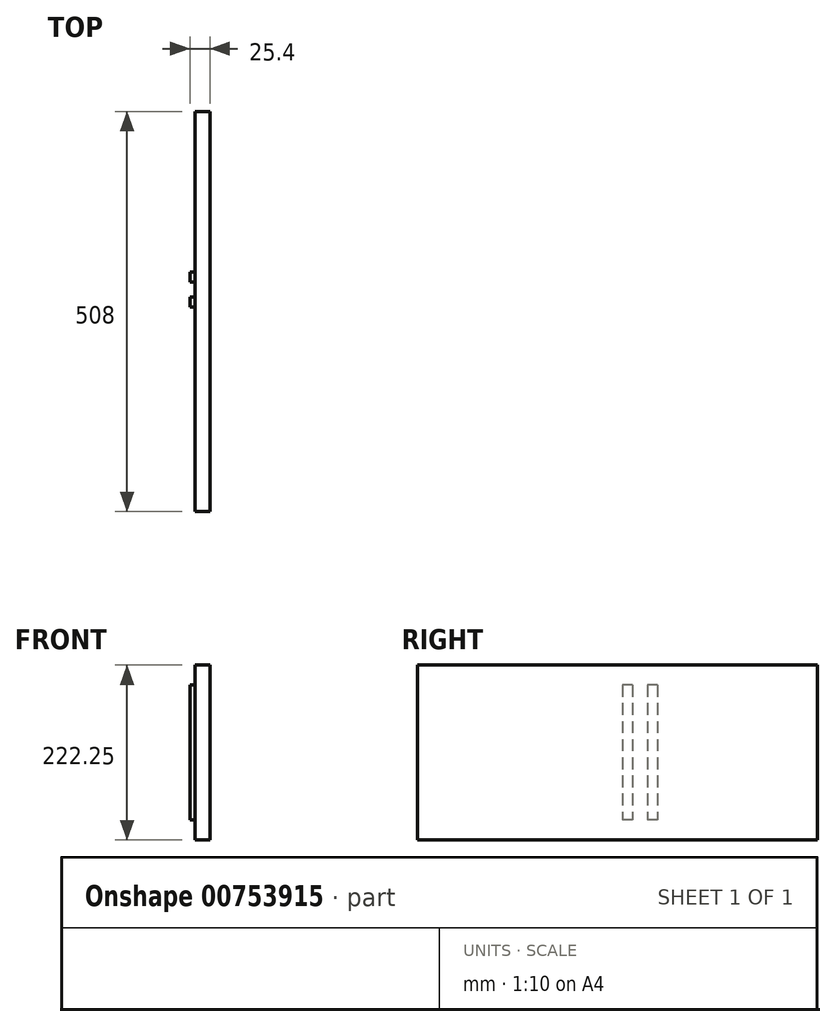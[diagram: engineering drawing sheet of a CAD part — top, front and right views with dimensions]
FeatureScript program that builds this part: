
annotation { "Feature Type Name" : "Feature", "Feature Type Description" : "" }
export const myFeature = defineFeature(function(context is Context, id is Id, definition is map)
    precondition{}
    {
        {
            var Q0;
            Q0=qCreatedBy(makeId("Right.planeOp"),FACE);
            var sketch = newSketch(context, id + "F0", { "sketchPlane" : qUnion([Q0])});
            skLineSegment(sketch, "E0.bottom", {"start": v(254, -111.12) * mm, "end": v(-254, -111.13) * mm});
            skLineSegment(sketch, "E0.top", {"start": v(254, 111.13) * mm, "end": v(-254, 111.12) * mm});
            skLineSegment(sketch, "E0.left", {"start": v(254, -111.12) * mm, "end": v(254, 111.13) * mm});
            skLineSegment(sketch, "E0.right", {"start": v(-254, -111.13) * mm, "end": v(-254, 111.12) * mm});
            skPoint(sketch, "E0.middle", {"position": v(0, 0) * mm});
            skLineSegment(sketch, "E1.0", {"start": v(253.65, 85.73) * mm, "end": v(-254, 85.72) * mm});
            skLineSegment(sketch, "E2.0", {"start": v(254, -85.72) * mm, "end": v(-254, -85.73) * mm});
            skLineSegment(sketch, "E3", {"start": v(253.65, 85.73) * mm, "end": v(50.45, 85.73) * mm});
            skLineSegment(sketch, "E4", {"start": v(50.45, 85.73) * mm, "end": v(37.75, 85.73) * mm});
            skLineSegment(sketch, "E5", {"start": v(37.75, 85.73) * mm, "end": v(18.7, 85.73) * mm});
            skLineSegment(sketch, "E6", {"start": v(18.7, 85.73) * mm, "end": v(6, 85.73) * mm});
            skLineSegment(sketch, "E7.bottom", {"start": v(6, 85.73) * mm, "end": v(18.7, 85.73) * mm});
            skLineSegment(sketch, "E7.top", {"start": v(6, -85.73) * mm, "end": v(18.7, -85.73) * mm});
            skLineSegment(sketch, "E7.left", {"start": v(6, 85.73) * mm, "end": v(6, -85.73) * mm});
            skLineSegment(sketch, "E7.right", {"start": v(18.7, 85.73) * mm, "end": v(18.7, -85.73) * mm});
            skLineSegment(sketch, "E8.bottom", {"start": v(37.75, 85.73) * mm, "end": v(50.45, 85.73) * mm});
            skLineSegment(sketch, "E8.top", {"start": v(37.75, -85.73) * mm, "end": v(50.45, -85.73) * mm});
            skLineSegment(sketch, "E8.left", {"start": v(37.75, 85.73) * mm, "end": v(37.75, -85.73) * mm});
            skLineSegment(sketch, "E8.right", {"start": v(50.45, 85.73) * mm, "end": v(50.45, -85.73) * mm});
            skSolve(sketch);
        }
        {
            var Q0;
            {var subQ0=sQuery(id+"F0.wireOp",EDGE,"E7.left");Q0=makeQuery(id+"F0.imprint","IMPRINT",FACE,{"disambiguationData":[TD([[makeQuery(id+"F0.imprint","IMPRINT",EDGE,{"derivedFrom":subQ0}),1.0]])]});}
            var Q1;
            {var subQ0=sQuery(id+"F0.wireOp",EDGE,"E8.left");Q1=makeQuery(id+"F0.imprint","IMPRINT",FACE,{"disambiguationData":[TD([[makeQuery(id+"F0.imprint","IMPRINT",EDGE,{"derivedFrom":subQ0}),1.0]])]});}
            extrude(context, id + "F1", {"entities" : qUnion([Q0, Q1]), "oppositeDirection" : true, "depth" : 6.35 * mm, "offsetDistance" : 25.4 * mm});
        }
        {
            var Q0;
            {var subQ5=sQuery(id+"F0.wireOp",EDGE,"E0.top");Q0=makeQuery(id+"F0.imprint","IMPRINT",FACE,{"disambiguationData":[TD([[makeQuery(id+"F0.imprint","IMPRINT",EDGE,{"derivedFrom":subQ5}),1.0]])]});}
            var Q1;
            {var subQ5=sQuery(id+"F0.wireOp",EDGE,"E7.left");Q1=makeQuery(id+"F0.imprint","IMPRINT",FACE,{"disambiguationData":[TD([[makeQuery(id+"F0.imprint","IMPRINT",EDGE,{"derivedFrom":subQ5}),-1.0]])]});}
            var Q2;
            {var subQ4=sQuery(id+"F0.wireOp",EDGE,"E0.bottom");Q2=makeQuery(id+"F0.imprint","IMPRINT",FACE,{"disambiguationData":[TD([[makeQuery(id+"F0.imprint","IMPRINT",EDGE,{"derivedFrom":subQ4}),-1.0]])]});}
            var Q3;
            {var subQ0=sQuery(id+"F0.wireOp",EDGE,"E7.left");Q3=makeQuery(id+"F0.imprint","IMPRINT",FACE,{"disambiguationData":[TD([[makeQuery(id+"F0.imprint","IMPRINT",EDGE,{"derivedFrom":subQ0}),1.0]])]});}
            var Q4;
            {var subQ2=sQuery(id+"F0.wireOp",EDGE,"E7.right");Q4=makeQuery(id+"F0.imprint","IMPRINT",FACE,{"disambiguationData":[TD([[makeQuery(id+"F0.imprint","IMPRINT",EDGE,{"derivedFrom":subQ2}),1.0]])]});}
            var Q5;
            {var subQ0=sQuery(id+"F0.wireOp",EDGE,"E8.left");Q5=makeQuery(id+"F0.imprint","IMPRINT",FACE,{"disambiguationData":[TD([[makeQuery(id+"F0.imprint","IMPRINT",EDGE,{"derivedFrom":subQ0}),1.0]])]});}
            extrude(context, id + "F2", {"entities" : qUnion([Q0, Q1, Q2, Q3, Q4, Q5]), "depth" : 19.05 * mm, "offsetDistance" : 25.4 * mm});
        }
    });
